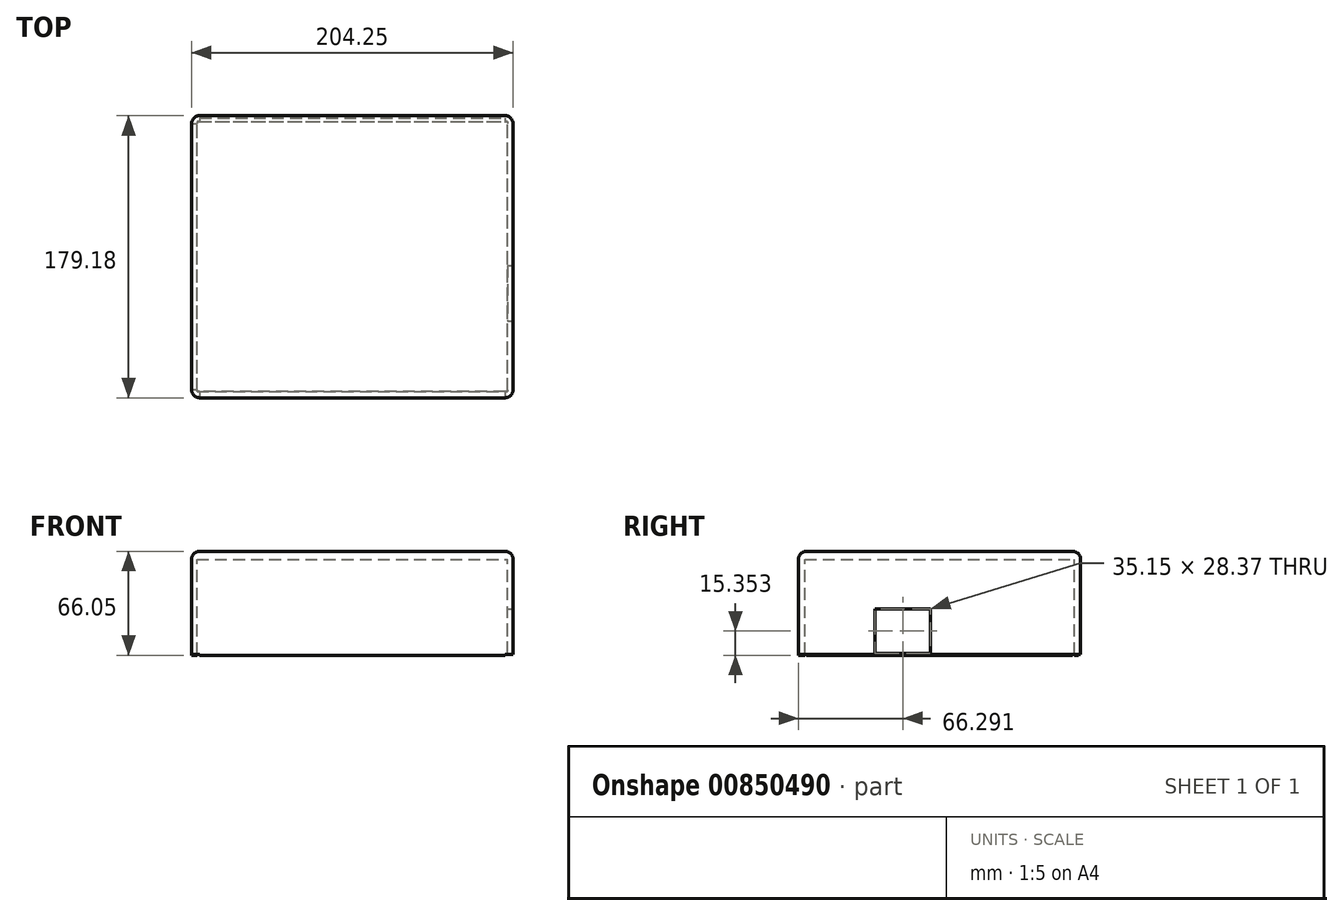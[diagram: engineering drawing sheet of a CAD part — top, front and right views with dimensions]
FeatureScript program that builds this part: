
annotation { "Feature Type Name" : "Feature", "Feature Type Description" : "" }
export const myFeature = defineFeature(function(context is Context, id is Id, definition is map)
    precondition{}
    {
        {
            var Q0;
            Q0=qCreatedBy(makeId("Top.planeOp"),FACE);
            var sketch = newSketch(context, id + "F0", { "sketchPlane" : qUnion([Q0])});
            skLineSegment(sketch, "E0.bottom", {"start": v(-88.03, -33.6) * mm, "end": v(116.22, -33.6) * mm});
            skLineSegment(sketch, "E0.top", {"start": v(-88.03, 145.57) * mm, "end": v(116.22, 145.57) * mm});
            skLineSegment(sketch, "E0.left", {"start": v(-88.03, -33.6) * mm, "end": v(-88.03, 145.57) * mm});
            skLineSegment(sketch, "E0.right", {"start": v(116.22, -33.6) * mm, "end": v(116.22, 145.57) * mm});
            skSolve(sketch);
        }
        {
            var Q0;
            Q0 = qSketchRegion(id + "F0", true);
            var Q1;
            Q1=makeQuery(id+"F0.imprint","IMPRINT",FACE,{"disambiguationData":[TD([[makeQuery(id+"F0.imprint","IMPRINT",EDGE,{"derivedFrom":sQuery(id+"F0.wireOp",EDGE,"E0.bottom")}),1.0]])]});
            extrude(context, id + "F1", {"entities" : qUnion([Q0, Q1]), "depth" : 63.5 * mm, "offsetDistance" : 25.4 * mm});
        }
        {
            var Q0;
            Q0=makeQuery(id+"F1.opExtrude","CAP_FACE",FACE,{"disambiguationData":[OSD([sQuery(id+"F0.wireOp",EDGE,"E0.bottom"),sQuery(id+"F0.wireOp",EDGE,"E0.top"),sQuery(id+"F0.wireOp",EDGE,"E0.left"),sQuery(id+"F0.wireOp",EDGE,"E0.right")])],"isStart":false});
            var sketch = newSketch(context, id + "F2", { "sketchPlane" : qUnion([Q0])});
            skLineSegment(sketch, "E1.bottom", {"start": v(-84.65, -29.56) * mm, "end": v(112.67, -29.56) * mm});
            skLineSegment(sketch, "E1.top", {"start": v(-84.65, 141.72) * mm, "end": v(112.67, 141.72) * mm});
            skLineSegment(sketch, "E1.left", {"start": v(-84.65, -29.56) * mm, "end": v(-84.65, 141.72) * mm});
            skLineSegment(sketch, "E1.right", {"start": v(112.67, -29.56) * mm, "end": v(112.67, 141.72) * mm});
            skSolve(sketch);
        }
        {
            var Q0;
            Q0=makeQuery(id+"F2.imprint","IMPRINT",FACE,{"disambiguationData":[TD([[makeQuery(id+"F2.imprint","IMPRINT",EDGE,{"derivedFrom":sQuery(id+"F2.wireOp",EDGE,"E1.bottom")}),1.0]])]});
            extrude(context, id + "F3", {"entities" : qUnion([Q0]), "operationType" : NewBodyOperationType.REMOVE, "oppositeDirection" : true, "depth" : 60.96 * mm, "offsetDistance" : 25.4 * mm});
        }
        {
            var Q0;
            Q0=makeQuery(id+"F1.opExtrude","CAP_FACE",FACE,{"disambiguationData":[OSD([sQuery(id+"F0.wireOp",EDGE,"E0.bottom"),sQuery(id+"F0.wireOp",EDGE,"E0.top"),sQuery(id+"F0.wireOp",EDGE,"E0.left"),sQuery(id+"F0.wireOp",EDGE,"E0.right")])],"isStart":false});
            var sketch = newSketch(context, id + "F4", { "sketchPlane" : qUnion([Q0])});
            skLineSegment(sketch, "E2.bottom", {"start": v(116.22, -33.6) * mm, "end": v(-88.03, -33.6) * mm});
            skLineSegment(sketch, "E2.top", {"start": v(116.22, 145.57) * mm, "end": v(-88.03, 145.57) * mm});
            skLineSegment(sketch, "E2.left", {"start": v(116.22, -33.6) * mm, "end": v(116.22, 145.57) * mm});
            skLineSegment(sketch, "E2.right", {"start": v(-88.03, -33.6) * mm, "end": v(-88.03, 145.57) * mm});
            skSolve(sketch);
        }
        {
            var Q0;
            Q0 = qSketchRegion(id + "F4", true);
            var Q1;
            Q1=makeQuery(id+"F4.imprint","IMPRINT",FACE,{"disambiguationData":[TD([[makeQuery(id+"F4.imprint","IMPRINT",EDGE,{"derivedFrom":makeQuery(id+"F3.boolean.opBoolean","COPY",EDGE,{"derivedFrom":makeQuery(id+"F3.opExtrude","CAP_EDGE",EDGE,{"disambiguationData":[OSD([sQuery(id+"F2.wireOp",EDGE,"E1.bottom")])],"isStart":true})})}),1.0]])]});
            extrude(context, id + "F5", {"entities" : qUnion([Q0, Q1]), "operationType" : NewBodyOperationType.ADD, "depth" : 5.08 * mm, "offsetDistance" : 25.4 * mm});
        }
        {
            var Q0;
            Q0=makeQuery(id+"F5.opExtrude","CAP_EDGE",EDGE,{"disambiguationData":[OSD([sQuery(id+"F4.wireOp",EDGE,"E2.left")])],"isStart":false});
            fillet(context, id + "F6", {"entities" : qUnion([Q0]), "radius" : 5.08 * mm, "tangentPropagation" : true, "allowEdgeOverflow" : false});
        }
        {
            var Q0;
            Q0=makeQuery(id+"F5.opExtrude","CAP_EDGE",EDGE,{"disambiguationData":[OSD([sQuery(id+"F4.wireOp",EDGE,"E2.top")])],"isStart":false});
            fillet(context, id + "F7", {"entities" : qUnion([Q0]), "radius" : 5.08 * mm, "tangentPropagation" : true, "allowEdgeOverflow" : false});
        }
        {
            var Q0;
            Q0=makeQuery(id+"F5.opExtrude","CAP_EDGE",EDGE,{"disambiguationData":[OSD([sQuery(id+"F4.wireOp",EDGE,"E2.bottom")])],"isStart":false});
            fillet(context, id + "F8", {"entities" : qUnion([Q0]), "radius" : 5.08 * mm, "tangentPropagation" : true, "allowEdgeOverflow" : false});
        }
        {
            var Q0;
            Q0=makeQuery(id+"F5.opExtrude","CAP_EDGE",EDGE,{"disambiguationData":[OSD([sQuery(id+"F4.wireOp",EDGE,"E2.right")])],"isStart":false});
            fillet(context, id + "F9", {"entities" : qUnion([Q0]), "radius" : 5.08 * mm, "tangentPropagation" : true, "allowEdgeOverflow" : false});
        }
        {
            var Q0;
            Q0=makeQuery(id+"F5.boolean.opBoolean","MERGE",FACE,{"derivedFrom":[makeQuery(id+"F1.opExtrude","SWEPT_FACE",FACE,{"disambiguationData":[OSD([sQuery(id+"F0.wireOp",EDGE,"E0.right")])]}),makeQuery(id+"F5.opExtrude","SWEPT_FACE",FACE,{"disambiguationData":[OSD([sQuery(id+"F4.wireOp",EDGE,"E2.left")])]})]});
            var sketch = newSketch(context, id + "F10", { "sketchPlane" : qUnion([Q0])});
            skLineSegment(sketch, "E3", {"start": v(-28.53, 0) * mm, "end": v(15.1, 0) * mm});
            skLineSegment(sketch, "E4", {"start": v(15.1, 0) * mm, "end": v(15.1, 3.7) * mm});
            skLineSegment(sketch, "E5", {"start": v(15.1, 3.7) * mm, "end": v(15.1, 32.07) * mm});
            skLineSegment(sketch, "E6", {"start": v(15.1, 32.07) * mm, "end": v(50.26, 32.07) * mm});
            skLineSegment(sketch, "E7", {"start": v(50.26, 32.07) * mm, "end": v(50.26, 3.7) * mm});
            skLineSegment(sketch, "E8", {"start": v(50.26, 3.7) * mm, "end": v(15.1, 3.7) * mm});
            skSolve(sketch);
        }
        {
            var Q0;
            Q0=makeQuery(id+"F10.imprint","IMPRINT",FACE,{"disambiguationData":[TD([[makeQuery(id+"F10.imprint","IMPRINT",EDGE,{"derivedFrom":sQuery(id+"F10.wireOp",EDGE,"E5")}),-1.0]])]});
            extrude(context, id + "F11", {"entities" : qUnion([Q0]), "operationType" : NewBodyOperationType.REMOVE, "oppositeDirection" : true, "depth" : 48.26 * mm, "offsetDistance" : 25.4 * mm});
        }
        {
            var Q0;
            Q0=makeQuery(id+"F5.boolean.opBoolean","MERGE",FACE,{"derivedFrom":[makeQuery(id+"F1.opExtrude","SWEPT_FACE",FACE,{"disambiguationData":[OSD([sQuery(id+"F0.wireOp",EDGE,"E0.bottom")])]}),makeQuery(id+"F5.opExtrude","SWEPT_FACE",FACE,{"disambiguationData":[OSD([sQuery(id+"F4.wireOp",EDGE,"E2.bottom")])]})]});
            var sketch = newSketch(context, id + "F12", { "sketchPlane" : qUnion([Q0])});
            skLineSegment(sketch, "E9", {"start": v(-82.95, 0) * mm, "end": v(-82.95, 2.53) * mm});
            skLineSegment(sketch, "E10", {"start": v(-82.95, 2.53) * mm, "end": v(111.14, 2.53) * mm});
            skSolve(sketch);
        }
        {
            var Q0;
            Q0=makeQuery(id+"F5.boolean.opBoolean","MERGE",FACE,{"derivedFrom":[makeQuery(id+"F1.opExtrude","SWEPT_FACE",FACE,{"disambiguationData":[OSD([sQuery(id+"F0.wireOp",EDGE,"E0.right")])]}),makeQuery(id+"F5.opExtrude","SWEPT_FACE",FACE,{"disambiguationData":[OSD([sQuery(id+"F4.wireOp",EDGE,"E2.left")])]})]});
            var sketch = newSketch(context, id + "F13", { "sketchPlane" : qUnion([Q0])});
            skLineSegment(sketch, "E11", {"start": v(-28.53, 0) * mm, "end": v(-28.53, 2.53) * mm});
            skLineSegment(sketch, "E12", {"start": v(-28.53, 2.53) * mm, "end": v(140.49, 2.53) * mm});
            skSolve(sketch);
        }
        {
            var Q0;
            {var subQ6=sQuery(id+"F13.wireOp",EDGE,"E12");Q0=makeQuery(id+"F13.imprint","IMPRINT",FACE,{"disambiguationData":[TD([[makeQuery(id+"F13.imprint","IMPRINT",EDGE,{"derivedFrom":subQ6}),1.0]])]});}
            var sketch = newSketch(context, id + "F14", { "sketchPlane" : qUnion([Q0])});
            skLineSegment(sketch, "E13.bottom", {"start": v(-28.53, 2.53) * mm, "end": v(140.5, 2.53) * mm});
            skLineSegment(sketch, "E13.top", {"start": v(-28.53, 0) * mm, "end": v(140.5, 0) * mm});
            skLineSegment(sketch, "E13.left", {"start": v(-28.53, 2.53) * mm, "end": v(-28.53, 0) * mm});
            skLineSegment(sketch, "E13.right", {"start": v(140.5, 2.53) * mm, "end": v(140.5, 0) * mm});
            skSolve(sketch);
        }
        {
            var Q0;
            Q0 = qSketchRegion(id + "F14", true);
            var Q1;
            Q1=makeQuery(id+"F13.imprint","IMPRINT",FACE,{"disambiguationData":[TD([[makeQuery(id+"F13.imprint","IMPRINT",EDGE,{"derivedFrom":sQuery(id+"F13.wireOp",EDGE,"E11")}),1.0]])]});
            extrude(context, id + "F15", {"entities" : qUnion([Q0, Q1]), "operationType" : NewBodyOperationType.REMOVE, "oppositeDirection" : true, "depth" : 212.34 * mm, "offsetDistance" : 25.4 * mm});
        }
        {
            var Q0;
            {var subQ0=sQuery(id+"F12.wireOp",EDGE,"E10");Q0=makeQuery(id+"F12.imprint","IMPRINT",FACE,{"disambiguationData":[TD([[makeQuery(id+"F12.imprint","IMPRINT",EDGE,{"derivedFrom":subQ0}),1.0]])]});}
            var sketch = newSketch(context, id + "F16", { "sketchPlane" : qUnion([Q0])});
            skLineSegment(sketch, "E14.bottom", {"start": v(-82.94, 2.53) * mm, "end": v(111.15, 2.53) * mm});
            skLineSegment(sketch, "E14.top", {"start": v(-82.94, 0) * mm, "end": v(111.15, 0) * mm});
            skLineSegment(sketch, "E14.left", {"start": v(-82.94, 2.53) * mm, "end": v(-82.94, 0) * mm});
            skLineSegment(sketch, "E14.right", {"start": v(111.15, 2.53) * mm, "end": v(111.15, 0) * mm});
            skSolve(sketch);
        }
        {
            var Q0;
            Q0 = qSketchRegion(id + "F16", true);
            var Q1;
            {var subQ2=sQuery(id+"F16.wireOp",EDGE,"E14.top");Q1=makeQuery(id+"F16.imprint","IMPRINT",FACE,{"disambiguationData":[TD([[makeQuery(id+"F16.imprint","IMPRINT",EDGE,{"derivedFrom":subQ2}),1.0]])]});}
            extrude(context, id + "F17", {"entities" : qUnion([Q0, Q1]), "operationType" : NewBodyOperationType.REMOVE, "oppositeDirection" : true, "depth" : 177.8 * mm, "offsetDistance" : 25.4 * mm});
        }
        {
            var Q0;
            Q0=makeQuery(id+"F15.boolean.opBoolean","COPY",FACE,{"derivedFrom":makeQuery(id+"F15.opExtrude","SWEPT_FACE",FACE,{"disambiguationData":[OSD([sQuery(id+"F14.wireOp",EDGE,"E13.bottom")])]})});
            var sketch = newSketch(context, id + "F18", { "sketchPlane" : qUnion([Q0])});
            skLineSegment(sketch, "E15.bottom", {"start": v(-88.03, 28.53) * mm, "end": v(116.22, 28.53) * mm});
            skLineSegment(sketch, "E15.top", {"start": v(-88.03, -140.5) * mm, "end": v(116.22, -140.5) * mm});
            skLineSegment(sketch, "E15.left", {"start": v(-88.03, 28.53) * mm, "end": v(-88.03, -140.5) * mm});
            skLineSegment(sketch, "E15.right", {"start": v(116.22, 28.53) * mm, "end": v(116.22, -140.5) * mm});
            skSolve(sketch);
        }
        {
            var Q0;
            {var subQ3=sQuery(id+"F18.wireOp",EDGE,"E15.bottom");Q0=makeQuery(id+"F18.imprint","IMPRINT",FACE,{"disambiguationData":[TD([[makeQuery(id+"F18.imprint","IMPRINT",EDGE,{"derivedFrom":subQ3}),-1.0]])]});}
            extrude(context, id + "F19", {"entities" : qUnion([Q0]), "operationType" : NewBodyOperationType.REMOVE, "oppositeDirection" : true, "depth" : 0.6 * mm, "offsetDistance" : 25.4 * mm});
        }
        {
            var Q0;
            {var subQ1=sQuery(id+"F0.wireOp",EDGE,"E0.left");var subQ2=sQuery(id+"F0.wireOp",EDGE,"E0.top");var subQ3=sQuery(id+"F0.wireOp",EDGE,"E0.right");Q0=makeQuery(id+"F15.boolean.opBoolean","SPLIT",FACE,{"disambiguationData":[TD([makeQuery(id+"F1.opExtrude","SWEPT_FACE",FACE,{"disambiguationData":[OSD([subQ2])]})])],"derivedFrom":makeQuery(id+"F1.opExtrude","CAP_FACE",FACE,{"disambiguationData":[OSD([sQuery(id+"F0.wireOp",EDGE,"E0.bottom"),subQ2,subQ1,subQ3])],"isStart":true})});}
            extrude(context, id + "F20", {"entities" : qUnion([Q0]), "operationType" : NewBodyOperationType.REMOVE, "oppositeDirection" : true, "depth" : 3.12 * mm, "offsetDistance" : 25.4 * mm});
        }
        {
            var Q0;
            {var subQ2=sQuery(id+"F0.wireOp",EDGE,"E0.left");var subQ3=sQuery(id+"F0.wireOp",EDGE,"E0.bottom");var subQ4=sQuery(id+"F0.wireOp",EDGE,"E0.right");Q0=makeQuery(id+"F15.boolean.opBoolean","SPLIT",FACE,{"disambiguationData":[TD([makeQuery(id+"F1.opExtrude","SWEPT_FACE",FACE,{"disambiguationData":[OSD([subQ3])]})])],"derivedFrom":makeQuery(id+"F1.opExtrude","CAP_FACE",FACE,{"disambiguationData":[OSD([subQ3,sQuery(id+"F0.wireOp",EDGE,"E0.top"),subQ2,subQ4])],"isStart":true})});}
            extrude(context, id + "F21", {"entities" : qUnion([Q0]), "operationType" : NewBodyOperationType.REMOVE, "oppositeDirection" : true, "depth" : 3.14 * mm, "offsetDistance" : 25.4 * mm});
        }
    });
